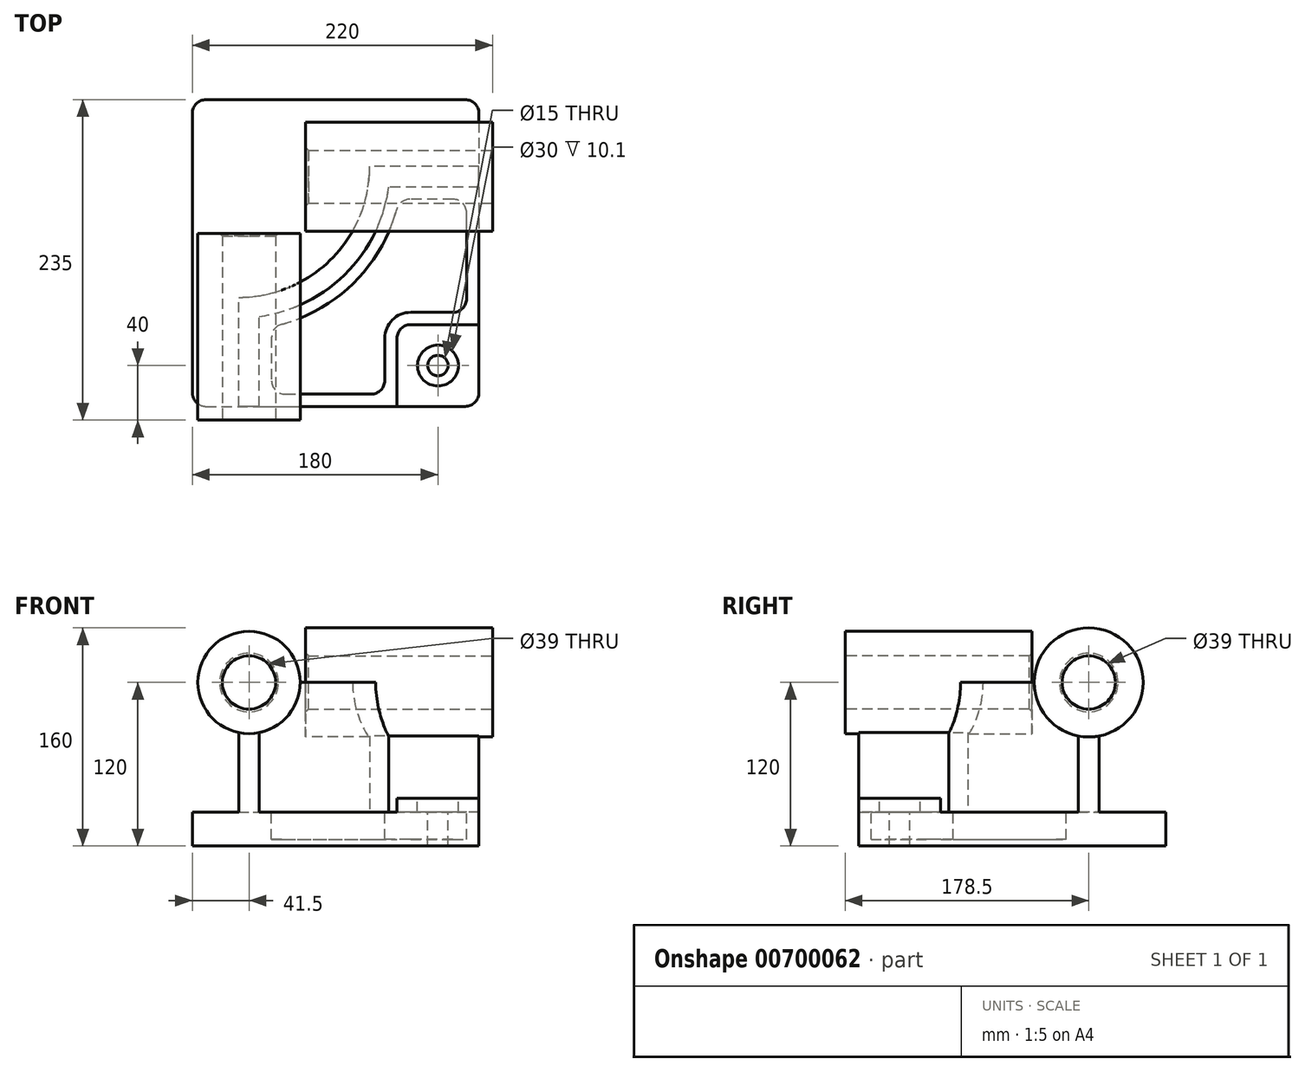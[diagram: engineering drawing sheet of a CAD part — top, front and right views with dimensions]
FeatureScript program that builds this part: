
annotation { "Feature Type Name" : "Feature", "Feature Type Description" : "" }
export const myFeature = defineFeature(function(context is Context, id is Id, definition is map)
    precondition{}
    {
        {
            var Q0;
            Q0=qCreatedBy(makeId("Top.planeOp"),FACE);
            var sketch = newSketch(context, id + "F0", { "sketchPlane" : qUnion([Q0])});
            skLineSegment(sketch, "E0.bottom", {"start": v(-105, 112.5) * mm, "end": v(105, 112.5) * mm});
            skLineSegment(sketch, "E0.top", {"start": v(-105, -112.5) * mm, "end": v(105, -112.5) * mm});
            skLineSegment(sketch, "E0.left", {"start": v(-105, 112.5) * mm, "end": v(-105, -112.5) * mm});
            skLineSegment(sketch, "E0.right", {"start": v(105, 112.5) * mm, "end": v(105, -112.5) * mm});
            skPoint(sketch, "E0.middle", {"position": v(0, 0) * mm});
            skSolve(sketch);
        }
        {
            var Q0;
            Q0=makeQuery(id+"F0.imprint","IMPRINT",FACE,{"disambiguationData":[TD([[makeQuery(id+"F0.imprint","IMPRINT",EDGE,{"derivedFrom":sQuery(id+"F0.wireOp",EDGE,"E0.bottom")}),-1.0]])]});
            extrude(context, id + "F1", {"entities" : qUnion([Q0]), "depth" : 25 * mm, "offsetDistance" : 25 * mm});
        }
        {
            var Q0;
            Q0=makeQuery(id+"F1.opExtrude","CAP_FACE",FACE,{"disambiguationData":[OSD([sQuery(id+"F0.wireOp",EDGE,"E0.bottom"),sQuery(id+"F0.wireOp",EDGE,"E0.top"),sQuery(id+"F0.wireOp",EDGE,"E0.left"),sQuery(id+"F0.wireOp",EDGE,"E0.right")])],"isStart":false});
            var sketch = newSketch(context, id + "F2", { "sketchPlane" : qUnion([Q0])});
            skLineSegment(sketch, "E1", {"start": v(-71, -112.5) * mm, "end": v(-71, -32.5) * mm});
            skLineSegment(sketch, "E2", {"start": v(105, 63.5) * mm, "end": v(25, 63.5) * mm});
            skArc(sketch, "E3", {"start": v(-71, -32.5) * mm, "mid": v(-3.12, -4.38) * mm, "end": v(25, 63.5) * mm});
            skLineSegment(sketch, "E4", {"start": v(-71, 63.5) * mm, "end": v(25, 63.5) * mm, "construction": true});
            skLineSegment(sketch, "E5", {"start": v(-71, 63.5) * mm, "end": v(-71, -32.5) * mm, "construction": true});
            skLineSegment(sketch, "E6.0", {"start": v(-56, -112.5) * mm, "end": v(-56, -46.48) * mm});
            skArc(sketch, "E6.1", {"start": v(-56, -46.48) * mm, "mid": v(7.49, -14.99) * mm, "end": v(38.98, 48.5) * mm});
            skLineSegment(sketch, "E6.2", {"start": v(105, 48.5) * mm, "end": v(38.98, 48.5) * mm});
            skLineSegment(sketch, "E7.0", {"start": v(-110, 117.5) * mm, "end": v(-110, -117.5) * mm});
            skLineSegment(sketch, "E7.1", {"start": v(110, 117.5) * mm, "end": v(-110, 117.5) * mm});
            skLineSegment(sketch, "E7.2", {"start": v(110, -117.5) * mm, "end": v(110, 117.5) * mm});
            skLineSegment(sketch, "E7.3", {"start": v(-110, -117.5) * mm, "end": v(110, -117.5) * mm});
            skLineSegment(sketch, "E8.0.0", {"start": v(-105, 112.5) * mm, "end": v(-105, -112.5) * mm});
            skLineSegment(sketch, "E8.0.1", {"start": v(-105, -112.5) * mm, "end": v(105, -112.5) * mm});
            skLineSegment(sketch, "E8.0.2", {"start": v(105, -112.5) * mm, "end": v(105, 112.5) * mm});
            skLineSegment(sketch, "E8.0.3", {"start": v(105, 112.5) * mm, "end": v(-105, 112.5) * mm});
            skSolve(sketch);
        }
        {
            var Q0;
            {var subQ3=sQuery(id+"F2.wireOp",EDGE,"E1");Q0=makeQuery(id+"F2.imprint","IMPRINT",FACE,{"disambiguationData":[TD([[makeQuery(id+"F2.imprint","IMPRINT",EDGE,{"derivedFrom":subQ3}),-1.0]])]});}
            extrude(context, id + "F3", {"entities" : qUnion([Q0]), "operationType" : NewBodyOperationType.ADD, "depth" : 95 * mm, "offsetDistance" : 25 * mm});
        }
        {
            var Q0;
            Q0=makeQuery(id+"F3.boolean.opBoolean","MERGE",FACE,{"derivedFrom":[makeQuery(id+"F1.opExtrude","SWEPT_FACE",FACE,{"disambiguationData":[OSD([sQuery(id+"F0.wireOp",EDGE,"E0.top")])]}),makeQuery(id+"F3.opExtrude","SWEPT_FACE",FACE,{"disambiguationData":[OSD([sQuery(id+"F2.wireOp",EDGE,"E8.0.1")])]})]});
            var sketch = newSketch(context, id + "F4", { "sketchPlane" : qUnion([Q0])});
            skCircle(sketch, "E9", {"center": v(-63.5, 120) * mm, "radius": 37.5 * mm});
            skSolve(sketch);
        }
        {
            var Q0;
            Q0 = qSketchRegion(id + "F4", true);
            extrude(context, id + "F5", {"entities" : qUnion([Q0]), "operationType" : NewBodyOperationType.ADD, "depth" : 10 * mm, "offsetDistance" : 25 * mm, "hasSecondDirection" : true, "secondDirectionOppositeDirection" : true, "secondDirectionDepth" : (137 - 10) * mm});
        }
        {
            var Q0;
            Q0=makeQuery(id+"F3.boolean.opBoolean","MERGE",FACE,{"derivedFrom":[makeQuery(id+"F1.opExtrude","SWEPT_FACE",FACE,{"disambiguationData":[OSD([sQuery(id+"F0.wireOp",EDGE,"E0.right")])]}),makeQuery(id+"F3.opExtrude","SWEPT_FACE",FACE,{"disambiguationData":[OSD([sQuery(id+"F2.wireOp",EDGE,"E8.0.2")])]})]});
            var sketch = newSketch(context, id + "F6", { "sketchPlane" : qUnion([Q0])});
            skCircle(sketch, "E10", {"center": v(56, 120) * mm, "radius": 40 * mm});
            skSolve(sketch);
        }
        {
            var Q0;
            Q0 = qSketchRegion(id + "F6", true);
            extrude(context, id + "F7", {"entities" : qUnion([Q0]), "operationType" : NewBodyOperationType.ADD, "depth" : 10 * mm, "offsetDistance" : 25 * mm, "hasSecondDirection" : true, "secondDirectionOppositeDirection" : true, "secondDirectionDepth" : (137 - 10) * mm});
        }
        {
            var Q0;
            {var subQ0=sQuery(id+"F0.wireOp",EDGE,"E0.right");var subQ1=sQuery(id+"F0.wireOp",EDGE,"E0.top");Q0=makeQuery(id+"F3.boolean.opBoolean","SPLIT",FACE,{"disambiguationData":[TD([makeQuery(id+"F3.opExtrude","SWEPT_FACE",FACE,{"disambiguationData":[OSD([sQuery(id+"F2.wireOp",EDGE,"E6.0")])]})])],"derivedFrom":makeQuery(id+"F1.opExtrude","CAP_FACE",FACE,{"disambiguationData":[OSD([sQuery(id+"F0.wireOp",EDGE,"E0.bottom"),subQ1,sQuery(id+"F0.wireOp",EDGE,"E0.left"),subQ0])],"isStart":false})});}
            var sketch = newSketch(context, id + "F8", { "sketchPlane" : qUnion([Q0])});
            skLineSegment(sketch, "E11.bottom", {"start": v(105, -112.5) * mm, "end": v(45, -112.5) * mm});
            skLineSegment(sketch, "E11.top", {"start": v(105, -52.5) * mm, "end": v(45, -52.5) * mm});
            skLineSegment(sketch, "E11.left", {"start": v(105, -112.5) * mm, "end": v(105, -52.5) * mm});
            skLineSegment(sketch, "E11.right", {"start": v(45, -112.5) * mm, "end": v(45, -52.5) * mm});
            skSolve(sketch);
        }
        {
            var Q0;
            Q0 = qSketchRegion(id + "F8", true);
            extrude(context, id + "F9", {"entities" : qUnion([Q0]), "operationType" : NewBodyOperationType.ADD, "depth" : (35 - 25) * mm, "offsetDistance" : 25 * mm});
        }
        {
            var Q0;
            Q0=makeQuery(id+"F9.opExtrude","SWEPT_EDGE",EDGE,{"disambiguationData":[OSD([sQuery(id+"F8.wireOp",EDGE,"E11.top"),sQuery(id+"F8.wireOp",EDGE,"E11.right")])]});
            fillet(context, id + "F10", {"entities" : qUnion([Q0]), "radius" : 10 * mm, "tangentPropagation" : true, "allowEdgeOverflow" : false});
        }
        {
            var Q0;
            {var subQ0=sQuery(id+"F0.wireOp",EDGE,"E0.right");var subQ1=sQuery(id+"F0.wireOp",EDGE,"E0.top");Q0=makeQuery(id+"F3.boolean.opBoolean","SPLIT",FACE,{"disambiguationData":[TD([makeQuery(id+"F3.opExtrude","SWEPT_FACE",FACE,{"disambiguationData":[OSD([sQuery(id+"F2.wireOp",EDGE,"E6.0")])]})])],"derivedFrom":makeQuery(id+"F1.opExtrude","CAP_FACE",FACE,{"disambiguationData":[OSD([sQuery(id+"F0.wireOp",EDGE,"E0.bottom"),subQ1,sQuery(id+"F0.wireOp",EDGE,"E0.left"),subQ0])],"isStart":false})});}
            var sketch = newSketch(context, id + "F11", { "sketchPlane" : qUnion([Q0])});
            skLineSegment(sketch, "E12.0", {"start": v(-47, -54.08) * mm, "end": v(-47, -103.5) * mm});
            skArc(sketch, "E12.1", {"start": v(46.58, 39.5) * mm, "mid": v(13.85, -21.35) * mm, "end": v(-47, -54.08) * mm});
            skLineSegment(sketch, "E12.2", {"start": v(-47, -103.5) * mm, "end": v(36, -103.5) * mm});
            skLineSegment(sketch, "E12.3", {"start": v(96, 39.5) * mm, "end": v(46.58, 39.5) * mm});
            skLineSegment(sketch, "E12.4", {"start": v(36, -103.5) * mm, "end": v(36, -62.5) * mm});
            skArc(sketch, "E12.5", {"start": v(36, -62.5) * mm, "mid": v(41.56, -49.06) * mm, "end": v(55, -43.5) * mm});
            skLineSegment(sketch, "E12.6", {"start": v(55, -43.5) * mm, "end": v(96, -43.5) * mm});
            skLineSegment(sketch, "E12.7", {"start": v(96, -43.5) * mm, "end": v(96, 39.5) * mm});
            skSolve(sketch);
        }
        {
            var Q0;
            Q0 = qSketchRegion(id + "F11", true);
            extrude(context, id + "F12", {"entities" : qUnion([Q0]), "operationType" : NewBodyOperationType.REMOVE, "oppositeDirection" : true, "depth" : (25 - 5) * mm, "offsetDistance" : 25 * mm});
        }
        {
            var Q0;
            Q0=makeQuery(id+"F9.opExtrude","CAP_FACE",FACE,{"disambiguationData":[OSD([sQuery(id+"F8.wireOp",EDGE,"E11.bottom"),sQuery(id+"F8.wireOp",EDGE,"E11.top"),sQuery(id+"F8.wireOp",EDGE,"E11.left"),sQuery(id+"F8.wireOp",EDGE,"E11.right")])],"isStart":false});
            var sketch = newSketch(context, id + "F13", { "sketchPlane" : qUnion([Q0])});
            skCircle(sketch, "E13", {"center": v(75, -82.5) * mm, "radius": 15 * mm});
            skSolve(sketch);
        }
        {
            var Q0;
            Q0=sQuery(id+"F13.wireOp",VERTEX,"E13.center");
            var Q1;
            Q1=makeQuery(id+"F1.opExtrude","SWEPT_BODY",BODY,{"disambiguationData":[OSD([sQuery(id+"F0.wireOp",EDGE,"E0.bottom"),sQuery(id+"F0.wireOp",EDGE,"E0.top"),sQuery(id+"F0.wireOp",EDGE,"E0.left"),sQuery(id+"F0.wireOp",EDGE,"E0.right")])]});
            hole(context, id + "F14", {"style" : HoleStyle.C_BORE, "endStyle" : HoleEndStyle.THROUGH, "holeDiameter" : 15 * mm, "cBoreDiameter" : 30 * mm, "cBoreDepth" : 10.1 * mm, "majorDiameter" : 5 * mm, "isTappedThrough" : true, "tappedDepth" : 12 * mm, "tapClearance" : 3, "locations" : qUnion([Q0]), "scope" : qUnion([Q1])});
        }
        {
            var Q0;
            Q0=makeQuery(id+"F12.boolean.opBoolean","COPY",EDGE,{"derivedFrom":makeQuery(id+"F12.opExtrude","SWEPT_EDGE",EDGE,{"disambiguationData":[OSD([sQuery(id+"F11.wireOp",EDGE,"E12.0"),sQuery(id+"F11.wireOp",EDGE,"E12.1")])]})});
            var Q1;
            Q1=makeQuery(id+"F12.boolean.opBoolean","COPY",EDGE,{"derivedFrom":makeQuery(id+"F12.opExtrude","SWEPT_EDGE",EDGE,{"disambiguationData":[OSD([sQuery(id+"F11.wireOp",EDGE,"E12.1"),sQuery(id+"F11.wireOp",EDGE,"E12.3")])]})});
            var Q2;
            Q2=makeQuery(id+"F12.boolean.opBoolean","COPY",EDGE,{"derivedFrom":makeQuery(id+"F12.opExtrude","SWEPT_EDGE",EDGE,{"disambiguationData":[OSD([sQuery(id+"F11.wireOp",EDGE,"E12.0"),sQuery(id+"F11.wireOp",EDGE,"E12.2")])]})});
            var Q3;
            Q3=makeQuery(id+"F12.boolean.opBoolean","COPY",EDGE,{"derivedFrom":makeQuery(id+"F12.opExtrude","SWEPT_EDGE",EDGE,{"disambiguationData":[OSD([sQuery(id+"F11.wireOp",EDGE,"E12.3"),sQuery(id+"F11.wireOp",EDGE,"E12.7")])]})});
            fillet(context, id + "F15", {"entities" : qUnion([Q0, Q1, Q2, Q3]), "radius" : 10 * mm, "tangentPropagation" : true, "allowEdgeOverflow" : false});
        }
        {
            var Q0;
            Q0=makeQuery(id+"F12.boolean.opBoolean","COPY",EDGE,{"derivedFrom":makeQuery(id+"F12.opExtrude","SWEPT_EDGE",EDGE,{"disambiguationData":[OSD([sQuery(id+"F11.wireOp",EDGE,"E12.6"),sQuery(id+"F11.wireOp",EDGE,"E12.7")])]})});
            var Q1;
            Q1=makeQuery(id+"F12.boolean.opBoolean","COPY",EDGE,{"derivedFrom":makeQuery(id+"F12.opExtrude","SWEPT_EDGE",EDGE,{"disambiguationData":[OSD([sQuery(id+"F11.wireOp",EDGE,"E12.2"),sQuery(id+"F11.wireOp",EDGE,"E12.4")])]})});
            fillet(context, id + "F16", {"entities" : qUnion([Q0, Q1]), "radius" : 10 * mm, "tangentPropagation" : true, "allowEdgeOverflow" : false});
        }
        {
            var Q0;
            Q0=makeQuery(id+"F5.opExtrude","CAP_FACE",FACE,{"disambiguationData":[OSD([sQuery(id+"F4.wireOp",EDGE,"E9")])],"isStart":false});
            var sketch = newSketch(context, id + "F17", { "sketchPlane" : qUnion([Q0])});
            skCircle(sketch, "E14", {"center": v(-63.5, 120) * mm, "radius": 19.5 * mm});
            skSolve(sketch);
        }
        {
            var Q0;
            Q0 = qSketchRegion(id + "F17", true);
            extrude(context, id + "F18", {"entities" : qUnion([Q0]), "operationType" : NewBodyOperationType.REMOVE, "endBound" : BoundingType.THROUGH_ALL, "oppositeDirection" : true, "depth" : 25 * mm, "offsetDistance" : 25 * mm});
        }
        {
            var Q0;
            Q0=makeQuery(id+"F7.opExtrude","CAP_FACE",FACE,{"disambiguationData":[OSD([sQuery(id+"F6.wireOp",EDGE,"E10")])],"isStart":false});
            var sketch = newSketch(context, id + "F19", { "sketchPlane" : qUnion([Q0])});
            skCircle(sketch, "E15", {"center": v(56, 120) * mm, "radius": 19.5 * mm});
            skSolve(sketch);
        }
        {
            var Q0;
            Q0 = qSketchRegion(id + "F19", true);
            extrude(context, id + "F20", {"entities" : qUnion([Q0]), "operationType" : NewBodyOperationType.REMOVE, "endBound" : BoundingType.THROUGH_ALL, "oppositeDirection" : true, "depth" : 25 * mm, "offsetDistance" : 25 * mm});
        }
        {
            var Q0;
            Q0=makeQuery(id+"F20.boolean.opBoolean","COPY",EDGE,{"derivedFrom":makeQuery(id+"F20.opExtrude","CAP_EDGE",EDGE,{"disambiguationData":[OSD([sQuery(id+"F19.wireOp",EDGE,"E15")])],"isStart":true})});
            var Q1;
            Q1=makeQuery(id+"F18.boolean.opBoolean","COPY",EDGE,{"derivedFrom":makeQuery(id+"F18.opExtrude","CAP_EDGE",EDGE,{"disambiguationData":[OSD([sQuery(id+"F17.wireOp",EDGE,"E14")])],"isStart":true})});
            var Q2;
            Q2=makeQuery(id+"F20.boolean.opBoolean","INTERSECT",EDGE,{"derivedFrom":[makeQuery(id+"F7.opExtrude","CAP_FACE",FACE,{"disambiguationData":[OSD([sQuery(id+"F6.wireOp",EDGE,"E10")])],"isStart":true}),makeQuery(id+"F20.opExtrude","SWEPT_FACE",FACE,{"disambiguationData":[OSD([sQuery(id+"F19.wireOp",EDGE,"E15")])]})]});
            var Q3;
            Q3=makeQuery(id+"F18.boolean.opBoolean","INTERSECT",EDGE,{"derivedFrom":[makeQuery(id+"F5.opExtrude","CAP_FACE",FACE,{"disambiguationData":[OSD([sQuery(id+"F4.wireOp",EDGE,"E9")])],"isStart":true}),makeQuery(id+"F18.opExtrude","SWEPT_FACE",FACE,{"disambiguationData":[OSD([sQuery(id+"F17.wireOp",EDGE,"E14")])]})]});
            chamfer(context, id + "F21", {"entities" : qUnion([Q0, Q1, Q2, Q3]), "width" : 2 * mm, "tangentPropagation" : true});
        }
        {
            var Q0;
            Q0=makeQuery(id+"F1.opExtrude","SWEPT_EDGE",EDGE,{"disambiguationData":[OSD([sQuery(id+"F0.wireOp",EDGE,"E0.top"),sQuery(id+"F0.wireOp",EDGE,"E0.left")])]});
            var Q1;
            Q1=makeQuery(id+"F9.boolean.opBoolean","MERGE",EDGE,{"derivedFrom":[makeQuery(id+"F1.opExtrude","SWEPT_EDGE",EDGE,{"disambiguationData":[OSD([sQuery(id+"F0.wireOp",EDGE,"E0.top"),sQuery(id+"F0.wireOp",EDGE,"E0.right")])]}),makeQuery(id+"F9.opExtrude","SWEPT_EDGE",EDGE,{"disambiguationData":[OSD([sQuery(id+"F8.wireOp",EDGE,"E11.bottom"),sQuery(id+"F8.wireOp",EDGE,"E11.left")])]})]});
            var Q2;
            Q2=makeQuery(id+"F1.opExtrude","SWEPT_EDGE",EDGE,{"disambiguationData":[OSD([sQuery(id+"F0.wireOp",EDGE,"E0.bottom"),sQuery(id+"F0.wireOp",EDGE,"E0.right")])]});
            var Q3;
            Q3=makeQuery(id+"F1.opExtrude","SWEPT_EDGE",EDGE,{"disambiguationData":[OSD([sQuery(id+"F0.wireOp",EDGE,"E0.bottom"),sQuery(id+"F0.wireOp",EDGE,"E0.left")])]});
            fillet(context, id + "F22", {"entities" : qUnion([Q0, Q1, Q2, Q3]), "radius" : 10 * mm, "tangentPropagation" : true, "allowEdgeOverflow" : false});
        }
    });
